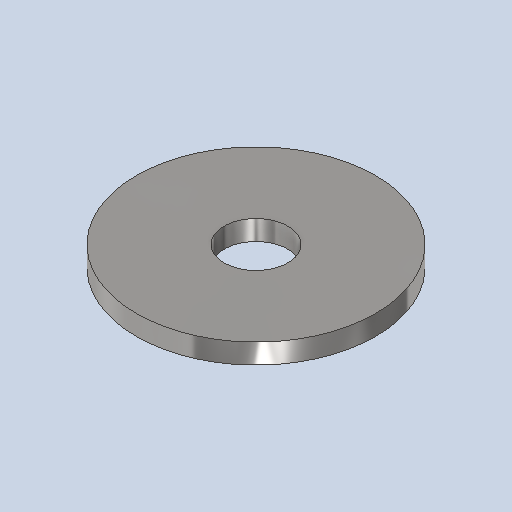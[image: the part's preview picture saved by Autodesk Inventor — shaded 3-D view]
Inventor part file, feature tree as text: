
AUTODESK INVENTOR PART (.ipt)
format: ipt  version: 2024.2 (Build 282272000, 272)  size: 108,032 bytes
history: native  units: mm
features: revolve x1, sketch x1
ambient origin geometry x8: Origin, YZ Plane, XZ Plane, XY Plane, X Axis, Y Axis, Z Axis, Center Point
bodies: Solid1 (feature_tree)
feature tree (2):
  revolve  "Revolution1"  [1 undecoded]
  sketch  "Sketch1"  dims[d5=90.0deg]
note: 1 required parameter value undecoded (feature->parameter linkage not recoverable at this tier; creation-order binding heuristic only, values carry confidence <= 0.55)
